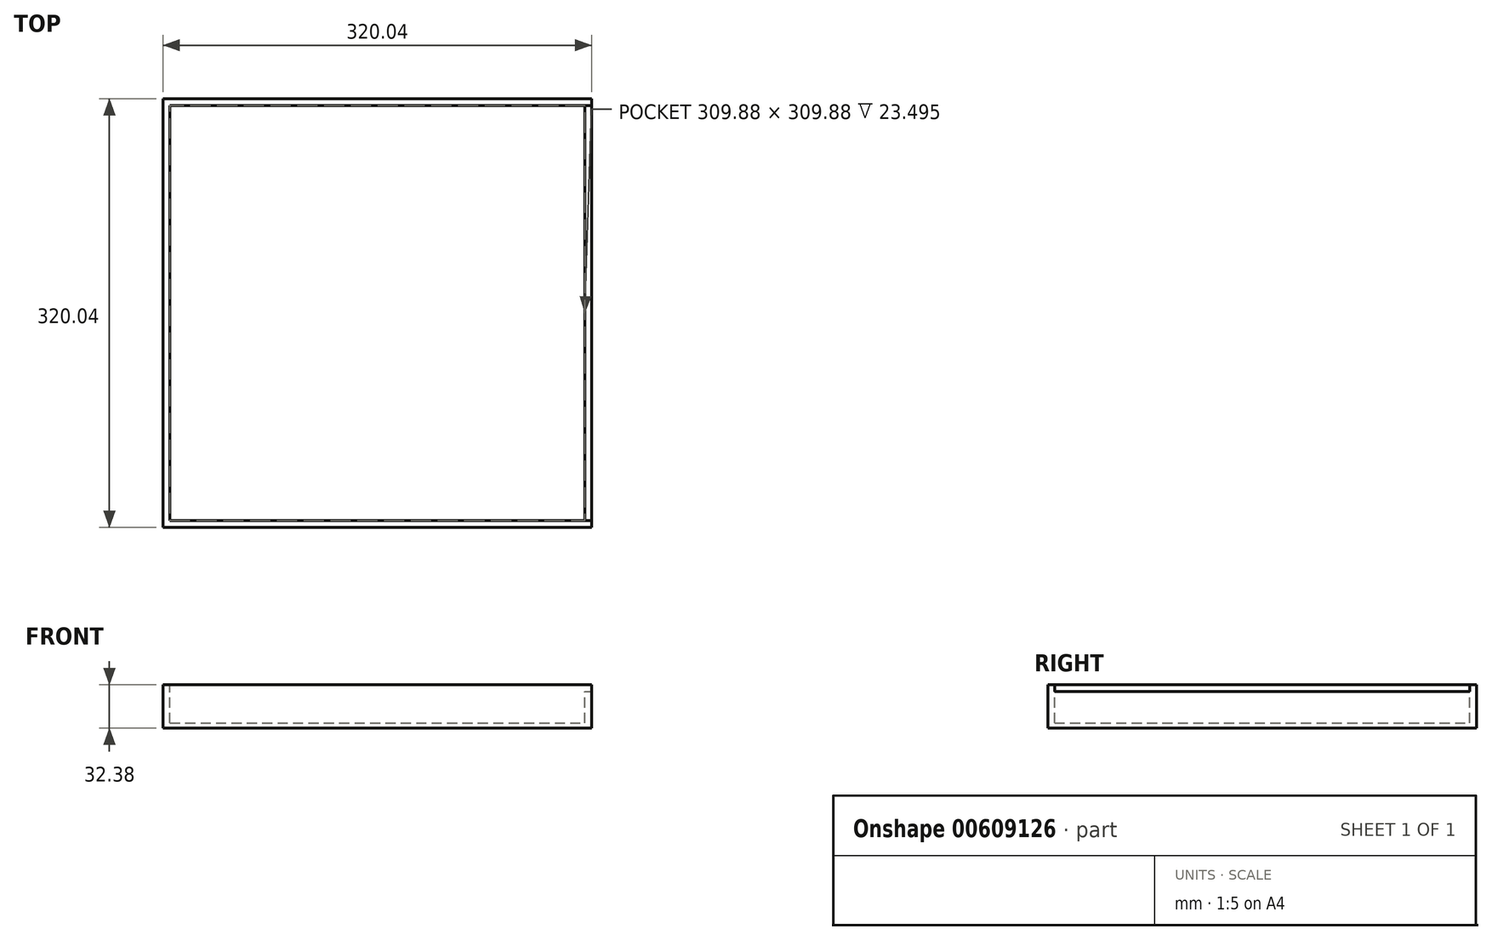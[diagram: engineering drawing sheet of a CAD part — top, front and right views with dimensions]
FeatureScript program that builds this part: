
annotation { "Feature Type Name" : "Feature", "Feature Type Description" : "" }
export const myFeature = defineFeature(function(context is Context, id is Id, definition is map)
    precondition{}
    {
        {
            var Q0;
            Q0=qCreatedBy(makeId("Top.planeOp"),FACE);
            var sketch = newSketch(context, id + "F0", { "sketchPlane" : qUnion([Q0])});
            skLineSegment(sketch, "E0.bottom", {"start": v(-160.02, -160.02) * mm, "end": v(160.02, -160.02) * mm});
            skLineSegment(sketch, "E0.top", {"start": v(-160.02, 160.02) * mm, "end": v(160.02, 160.02) * mm});
            skLineSegment(sketch, "E0.left", {"start": v(-160.02, -160.02) * mm, "end": v(-160.02, 160.02) * mm});
            skLineSegment(sketch, "E0.right", {"start": v(160.02, -160.02) * mm, "end": v(160.02, 160.02) * mm});
            skPoint(sketch, "E0.middle", {"position": v(0, 0) * mm});
            skSolve(sketch);
        }
        {
            var Q0;
            Q0 = qSketchRegion(id + "F0", true);
            extrude(context, id + "F1", {"entities" : qUnion([Q0]), "depth" : 32.38 * mm, "offsetDistance" : 25.4 * mm});
        }
        {
            var Q0;
            Q0=makeQuery(id+"F1.opExtrude","CAP_FACE",FACE,{"disambiguationData":[OSD([sQuery(id+"F0.wireOp",EDGE,"E0.bottom"),sQuery(id+"F0.wireOp",EDGE,"E0.top"),sQuery(id+"F0.wireOp",EDGE,"E0.left"),sQuery(id+"F0.wireOp",EDGE,"E0.right")])],"isStart":false});
            var sketch = newSketch(context, id + "F2", { "sketchPlane" : qUnion([Q0])});
            skLineSegment(sketch, "E1.bottom", {"start": v(-154.94, -154.94) * mm, "end": v(154.94, -154.94) * mm});
            skLineSegment(sketch, "E1.top", {"start": v(-154.94, 154.94) * mm, "end": v(154.94, 154.94) * mm});
            skLineSegment(sketch, "E1.left", {"start": v(-154.94, -154.94) * mm, "end": v(-154.94, 154.94) * mm});
            skLineSegment(sketch, "E1.right", {"start": v(154.94, -154.94) * mm, "end": v(154.94, 154.94) * mm});
            skPoint(sketch, "E1.middle", {"position": v(0, 0) * mm});
            skSolve(sketch);
        }
        {
            var Q0;
            Q0 = qSketchRegion(id + "F2", true);
            extrude(context, id + "F3", {"entities" : qUnion([Q0]), "operationType" : NewBodyOperationType.REMOVE, "oppositeDirection" : true, "depth" : 28.57 * mm, "offsetDistance" : 25.4 * mm});
        }
        {
            var Q0;
            Q0=makeQuery(id+"F1.opExtrude","CAP_FACE",FACE,{"disambiguationData":[OSD([sQuery(id+"F0.wireOp",EDGE,"E0.bottom"),sQuery(id+"F0.wireOp",EDGE,"E0.top"),sQuery(id+"F0.wireOp",EDGE,"E0.left"),sQuery(id+"F0.wireOp",EDGE,"E0.right")])],"isStart":false});
            var sketch = newSketch(context, id + "F4", { "sketchPlane" : qUnion([Q0])});
            skLineSegment(sketch, "E2.bottom", {"start": v(154.94, 154.94) * mm, "end": v(160.02, 154.94) * mm});
            skLineSegment(sketch, "E2.top", {"start": v(154.94, -154.94) * mm, "end": v(160.02, -154.94) * mm});
            skLineSegment(sketch, "E2.left", {"start": v(154.94, 154.94) * mm, "end": v(154.94, -154.94) * mm});
            skLineSegment(sketch, "E2.right", {"start": v(160.02, 154.94) * mm, "end": v(160.02, -154.94) * mm});
            skSolve(sketch);
        }
        {
            var Q0;
            Q0=makeQuery(id+"F4.imprint","IMPRINT",FACE,{"disambiguationData":[TD([[makeQuery(id+"F4.imprint","IMPRINT",EDGE,{"derivedFrom":sQuery(id+"F4.wireOp",EDGE,"E2.bottom")}),-1.0]])]});
            extrude(context, id + "F5", {"entities" : qUnion([Q0]), "operationType" : NewBodyOperationType.REMOVE, "oppositeDirection" : true, "depth" : 5.08 * mm, "offsetDistance" : 25.4 * mm});
        }
    });
